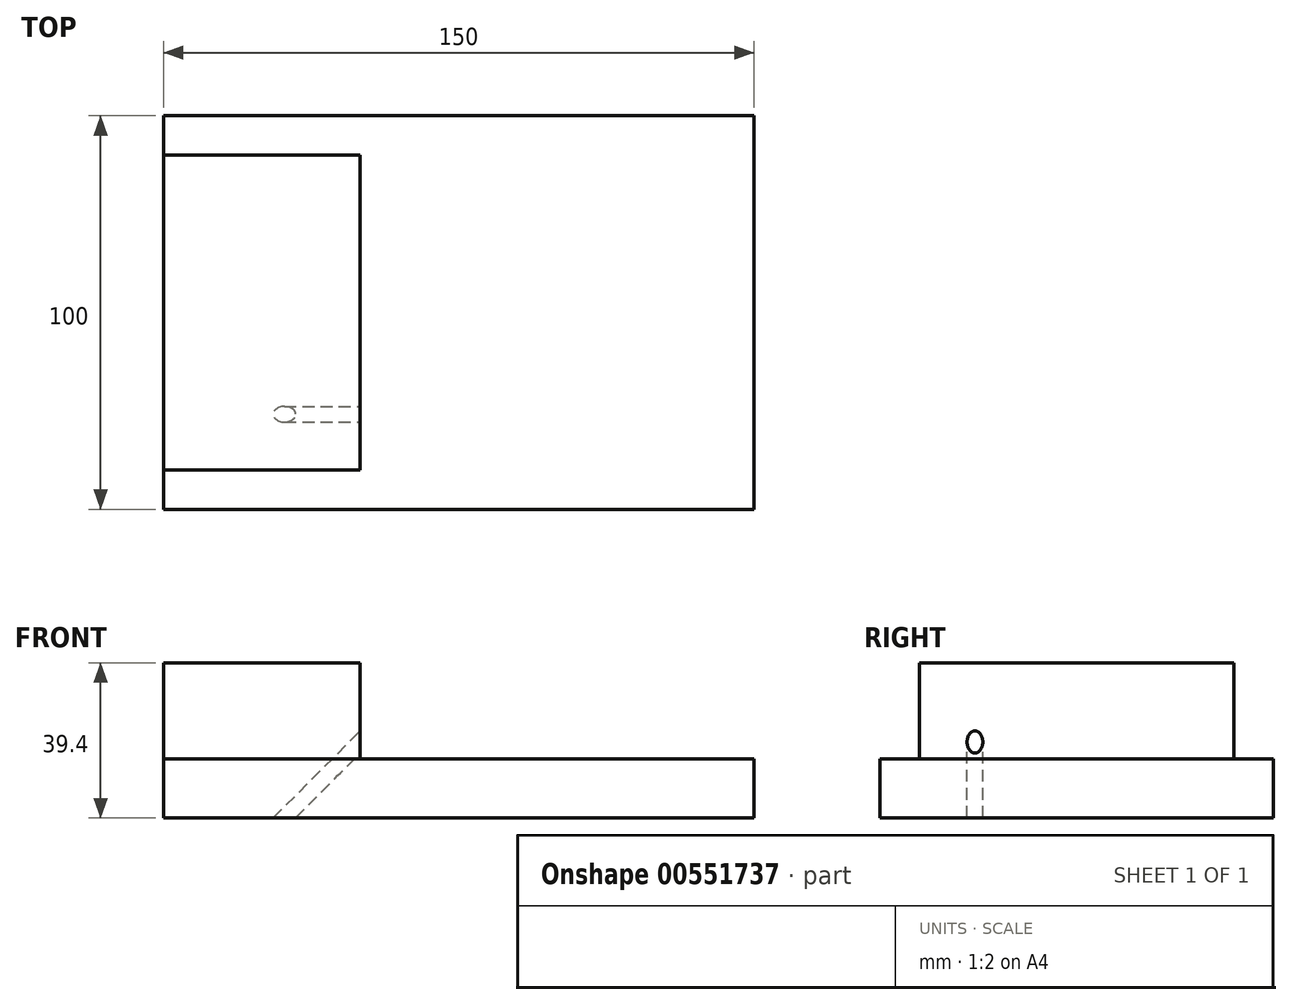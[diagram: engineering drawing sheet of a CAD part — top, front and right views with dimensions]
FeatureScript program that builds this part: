
annotation { "Feature Type Name" : "Feature", "Feature Type Description" : "" }
export const myFeature = defineFeature(function(context is Context, id is Id, definition is map)
    precondition{}
    {
        {
            var Q0;
            Q0=qCreatedBy(makeId("Top.planeOp"),FACE);
            var sketch = newSketch(context, id + "F0", { "sketchPlane" : qUnion([Q0])});
            skLineSegment(sketch, "E0.bottom", {"start": v(75, -50) * mm, "end": v(-75, -50) * mm});
            skLineSegment(sketch, "E0.top", {"start": v(75, 50) * mm, "end": v(-75, 50) * mm});
            skLineSegment(sketch, "E0.left", {"start": v(75, -50) * mm, "end": v(75, 50) * mm});
            skLineSegment(sketch, "E0.right", {"start": v(-75, -50) * mm, "end": v(-75, 50) * mm});
            skPoint(sketch, "E0.middle", {"position": v(0, 0) * mm});
            skSolve(sketch);
        }
        {
            var Q0;
            Q0 = qSketchRegion(id + "F0", true);
            extrude(context, id + "F1", {"entities" : qUnion([Q0]), "depth" : 15 * mm, "offsetDistance" : 25 * mm});
        }
        {
            var Q0;
            Q0=makeQuery(id+"F1.opExtrude","CAP_FACE",FACE,{"disambiguationData":[OSD([sQuery(id+"F0.wireOp",EDGE,"E0.bottom"),sQuery(id+"F0.wireOp",EDGE,"E0.top"),sQuery(id+"F0.wireOp",EDGE,"E0.left"),sQuery(id+"F0.wireOp",EDGE,"E0.right")])],"isStart":false});
            var sketch = newSketch(context, id + "F2", { "sketchPlane" : qUnion([Q0])});
            skLineSegment(sketch, "E1.bottom", {"start": v(-75, 40) * mm, "end": v(-25, 40) * mm});
            skLineSegment(sketch, "E1.top", {"start": v(-75, -40) * mm, "end": v(-25, -40) * mm});
            skLineSegment(sketch, "E1.left", {"start": v(-75, 40) * mm, "end": v(-75, -40) * mm});
            skLineSegment(sketch, "E1.right", {"start": v(-25, 40) * mm, "end": v(-25, -40) * mm});
            skSolve(sketch);
        }
        {
            var Q0;
            Q0 = qSketchRegion(id + "F2", true);
            extrude(context, id + "F3", {"entities" : qUnion([Q0]), "operationType" : NewBodyOperationType.ADD, "depth" : 24.4 * mm, "offsetDistance" : 25 * mm});
        }
        {
            var Q0;
            Q0=makeQuery(id+"F3.opExtrude","CAP_EDGE",EDGE,{"disambiguationData":[OSD([sQuery(id+"F2.wireOp",EDGE,"E1.right")])],"isStart":false});
            cPlane(context, id + "F4", {"entities" : qUnion([Q0]), "cplaneType" : CPlaneType.LINE_ANGLE, "offset" : 25 * mm, "angle" : 315 * degree, "width" : 150 * mm, "height" : 150 * mm});
        }
        {
            var Q0;
            Q0=qCreatedBy(id+"F4.planeOp",FACE);
            var sketch = newSketch(context, id + "F5", { "sketchPlane" : qUnion([Q0])});
            skCircle(sketch, "E2", {"center": v(25.85, 31.3) * mm, "radius": 2 * mm});
            skSolve(sketch);
        }
        {
            var Q0;
            Q0 = qSketchRegion(id + "F5", true);
            extrude(context, id + "F6", {"entities" : qUnion([Q0]), "operationType" : NewBodyOperationType.REMOVE, "depth" : 64.2 * mm, "offsetDistance" : 25 * mm});
        }
    });
